# Revit family: Return-Teknion-CWRR_Teknion_Reception-R2016
name_source: partatom
category: Furniture
revit_build: Autodesk Revit 2018 (Build: 20190510_1515(x64)
units: mm (PartAtom-declared; Revit-internal decimal feet)

## family parameters
Always vertical = Yes
Cut with Voids When Loaded = No
OmniClass Number = 23.40.20.00
OmniClass Title = General Furniture and Specialties
Room Calculation Point = No
Shared = Yes
Work Plane-Based = No

## types (3) — shared parameters
Assembly Code = E2020200
Base Finish = Source Laminate - Teknion - RV - Very White
Base Finish Note = Choose a between a Foundation Laminate, Flintwood, or Veneer Finish below.
For Additional Finishes, please visit = https://assets.teknion.com
Manufacturer = Teknion
Manufacturer Fax = 416.661.4586
Part Number = CWRR
Product Documentation Link = https://assets.teknion.com
Product Line = Teknion Reception
Product Page URL = https://www.teknion.com
Series = Custom Wood
Sustainability Data = https://www.teknion.com
To render, please download texture images found here = https://assets.teknion.com
Top Finish = Veneer-Teknion-5T-Flintwood-White_Truffle
URL = www.teknion.com
Unit Weight URL = http://www.teknion.com
Warranty = http://www.teknion.com

## per-type parameters (varying)
| type | Description | Front & Back Gable Left Offset | Front & Back Gable Right Offset | Left Connection, 1 End Gable | Left Gable Back Offset | Left Gable Finish | Left Gable Finish Note | Model | No Connection, 2 End Gables | Right Connection, 1 End Gable | Right Gable Back Offset | Right Gable Finish | Right Gable Finish Note |
| Has Right Connection, 1 End Gable | Teknion Reception Return, Right Connection, 1 End Gable, 29" Height | 1.039 " | 0 " | No | 0 " | Veneer-Teknion-5T-Flintwood-White_Truffle | Please choose a Flintwood or Veneer Finish below. | CWRR29__R | No | Yes | 1.039 " | Source Laminate - Teknion - RV - Very White | Match Base Finish. |
| Has Left Connection, 1 End Gable | Teknion Reception Return, Left Connection, 1 End Gable, 29" Height | 0 " | 1.039 " | Yes | 1.039 " | Source Laminate - Teknion - RV - Very White | Match Base Finish. | CWRR29__L | No | No | 0 " | Veneer-Teknion-5T-Flintwood-White_Truffle | Please choose a Flintwood or Veneer Finish below. |
| Has No Connection, 2 End Gables | Teknion Reception Return, No Connection, 2 End Gables | 1.039 " | 1.039 " | No | 0 " | Veneer-Teknion-5T-Flintwood-White_Truffle | Please choose a Flintwood or Veneer Finish below. | CWRR___N | Yes | No | 0 " | Veneer-Teknion-5T-Flintwood-White_Truffle | Please choose a Flintwood or Veneer Finish below. |

## geometry (parser evidence)
native form markers: Sweep x2
no freeform markers — native parametric forms only
